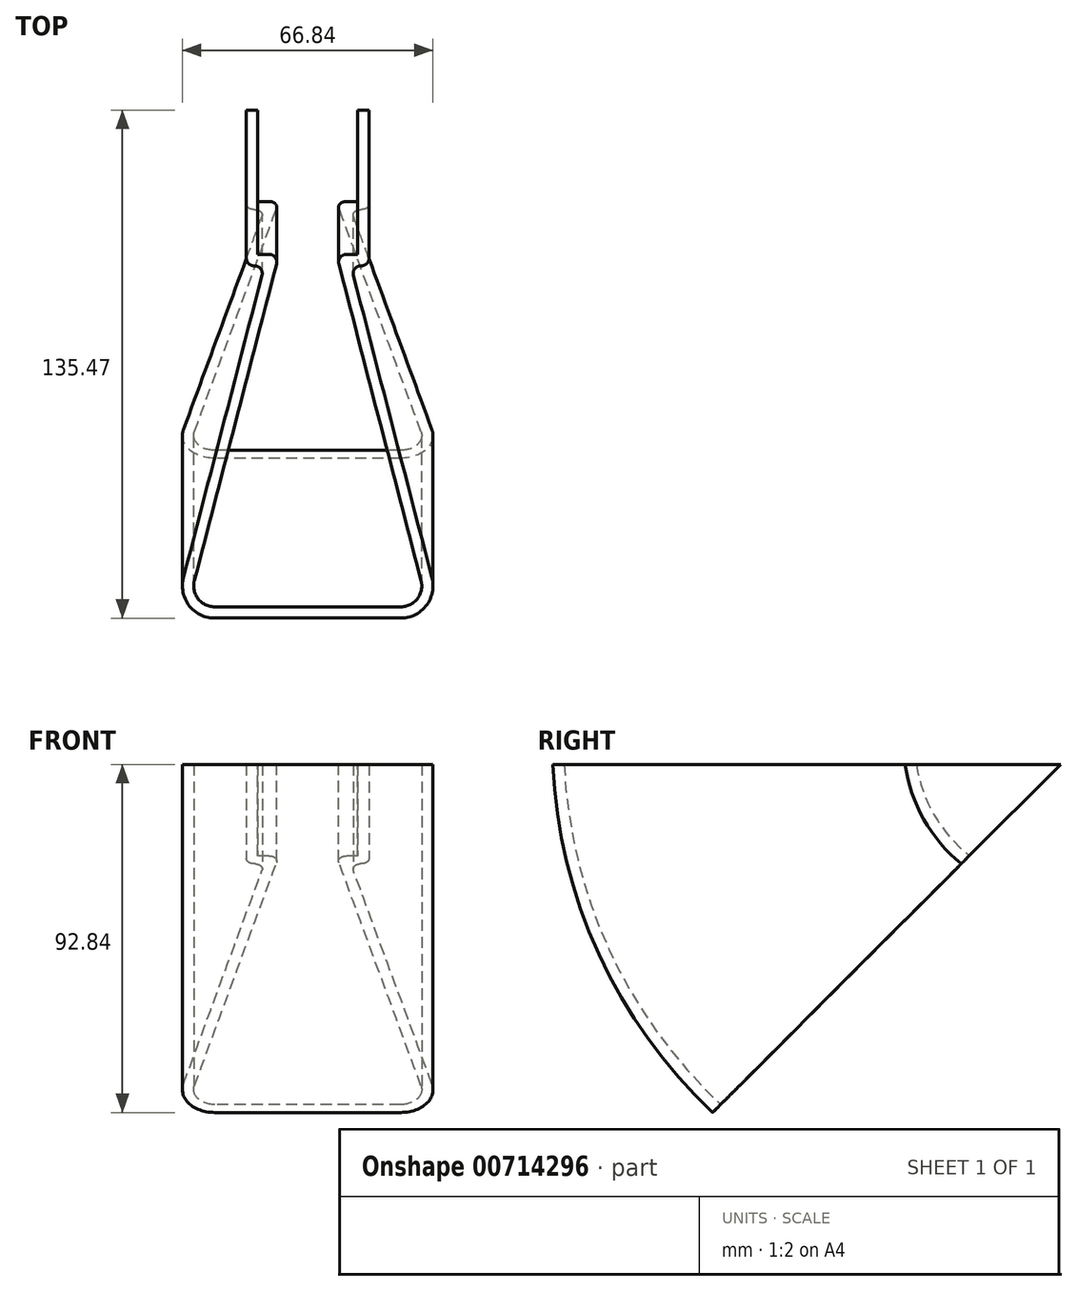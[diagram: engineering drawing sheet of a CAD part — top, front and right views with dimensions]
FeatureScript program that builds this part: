
annotation { "Feature Type Name" : "Feature", "Feature Type Description" : "" }
export const myFeature = defineFeature(function(context is Context, id is Id, definition is map)
    precondition{}
    {
        {
            var Q0;
            Q0=qCreatedBy(makeId("Top.planeOp"),FACE);
            var sketch = newSketch(context, id + "F0", { "sketchPlane" : qUnion([Q0])});
            skLineSegment(sketch, "E0", {"start": v(-5.5, 0) * mm, "end": v(5.5, 0) * mm, "construction": true});
            skLineSegment(sketch, "E1", {"start": v(-24.82, -94) * mm, "end": v(24.82, -94) * mm, "construction": true});
            skLineSegment(sketch, "E2", {"start": v(0, 0) * mm, "end": v(0, -94) * mm, "construction": true});
            skLineSegment(sketch, "E3", {"start": v(-5.5, 0) * mm, "end": v(-28.7, -89) * mm, "construction": true});
            skLineSegment(sketch, "E4", {"start": v(5.5, 0) * mm, "end": v(28.7, -89) * mm, "construction": true});
            skPoint(sketch, "E5.visualSharp", {"position": v(-30, -94) * mm});
            skArc(sketch, "E5.filletArc", {"start": v(-28.7, -89) * mm, "mid": v(-27.99, -92.45) * mm, "end": v(-24.82, -94) * mm, "construction": true});
            skPoint(sketch, "E6.visualSharp", {"position": v(30, -94) * mm});
            skArc(sketch, "E6.filletArc", {"start": v(24.82, -94) * mm, "mid": v(27.99, -92.45) * mm, "end": v(28.7, -89) * mm, "construction": true});
            skLineSegment(sketch, "E7.0", {"start": v(7.68, -2.03) * mm, "end": v(30.24, -88.59) * mm});
            skLineSegment(sketch, "E7.1", {"start": v(-7.68, -2.03) * mm, "end": v(-30.24, -88.59) * mm});
            skArc(sketch, "E7.2", {"start": v(-30.24, -88.59) * mm, "mid": v(-29.25, -93.42) * mm, "end": v(-24.82, -95.6) * mm});
            skLineSegment(sketch, "E7.3", {"start": v(-24.82, -95.6) * mm, "end": v(24.82, -95.6) * mm});
            skArc(sketch, "E7.4", {"start": v(24.82, -95.6) * mm, "mid": v(29.25, -93.42) * mm, "end": v(30.24, -88.59) * mm});
            skLineSegment(sketch, "E8", {"start": v(-5.5, 0) * mm, "end": v(-7.15, 0) * mm, "construction": true});
            skLineSegment(sketch, "E9", {"start": v(5.5, 0) * mm, "end": v(7.15, 0) * mm, "construction": true});
            skLineSegment(sketch, "E10.0", {"start": v(11.54, -4.95) * mm, "end": v(33.15, -87.83) * mm});
            skLineSegment(sketch, "E10.1", {"start": v(-11.54, -4.95) * mm, "end": v(-33.15, -87.83) * mm});
            skArc(sketch, "E10.2", {"start": v(-33.15, -87.83) * mm, "mid": v(-31.63, -95.26) * mm, "end": v(-24.82, -98.6) * mm});
            skLineSegment(sketch, "E10.3", {"start": v(-24.82, -98.6) * mm, "end": v(24.82, -98.6) * mm});
            skArc(sketch, "E10.4", {"start": v(24.82, -98.6) * mm, "mid": v(31.63, -95.26) * mm, "end": v(33.15, -87.83) * mm});
            skLineSegment(sketch, "E11", {"start": v(7.15, 0) * mm, "end": v(10.25, 0) * mm, "construction": true});
            skLineSegment(sketch, "E12", {"start": v(0, 0) * mm, "end": v(0, 37) * mm, "construction": true});
            skLineSegment(sketch, "E13", {"start": v(-19.77, 37) * mm, "end": v(21.2, 37) * mm, "construction": true});
            skLineSegment(sketch, "E14", {"start": v(10.25, 0) * mm, "end": v(11.75, 0) * mm, "construction": true});
            skLineSegment(sketch, "E15", {"start": v(11.75, 0) * mm, "end": v(11.75, 37) * mm, "construction": true});
            skLineSegment(sketch, "E16.0", {"start": v(5.5, 0) * mm, "end": v(6.32, 0) * mm});
            skLineSegment(sketch, "E16.1", {"start": v(-5.5, 0) * mm, "end": v(5.5, 0) * mm});
            skLineSegment(sketch, "E17.0", {"start": v(13.35, -1.95) * mm, "end": v(13.35, 37) * mm});
            skLineSegment(sketch, "E17.3", {"start": v(7.68, -2.03) * mm, "end": v(9.62, -1.95) * mm});
            skLineSegment(sketch, "E17.4", {"start": v(9.62, -1.95) * mm, "end": v(13.35, -1.95) * mm});
            skLineSegment(sketch, "E18.0", {"start": v(16.35, -4.95) * mm, "end": v(16.35, 37) * mm});
            skLineSegment(sketch, "E18.4", {"start": v(11.54, -4.95) * mm, "end": v(16.35, -4.95) * mm});
            skLineSegment(sketch, "E19", {"start": v(16.35, 37) * mm, "end": v(13.35, 37) * mm});
            skLineSegment(sketch, "E20.MirrorCS", {"start": v(-16.35, -4.95) * mm, "end": v(-16.35, 37) * mm});
            skLineSegment(sketch, "E21.MirrorCS", {"start": v(-13.35, -1.95) * mm, "end": v(-13.35, 37) * mm});
            skLineSegment(sketch, "E22.MirrorCS", {"start": v(-9.62, -1.95) * mm, "end": v(-13.35, -1.95) * mm});
            skLineSegment(sketch, "E23.MirrorCS", {"start": v(-11.54, -4.95) * mm, "end": v(-16.35, -4.95) * mm});
            skLineSegment(sketch, "E24.MirrorCS", {"start": v(-7.68, -2.03) * mm, "end": v(-9.62, -1.95) * mm});
            skLineSegment(sketch, "E25.MirrorCS", {"start": v(-16.35, 37) * mm, "end": v(-13.35, 37) * mm});
            skPoint(sketch, "E26.trimOffspring.end.orphan", {"position": v(9.62, -4.95) * mm});
            skPoint(sketch, "E26.trimOffspring.start.orphan", {"position": v(8.34, -4.57) * mm});
            skPoint(sketch, "E27.orphan", {"position": v(-9.62, -4.95) * mm});
            skPoint(sketch, "E28.MirrorCS.start.orphan", {"position": v(-8.34, -4.57) * mm});
            skSolve(sketch);
        }
        {
            var Q0;
            Q0=makeQuery(id+"F0.imprint","IMPRINT",FACE,{"disambiguationData":[TD([[makeQuery(id+"F0.imprint","IMPRINT",EDGE,{"derivedFrom":sQuery(id+"F0.wireOp",EDGE,"E7.0")}),1.0]])]});
            var Q1;
            Q1=sQuery(id+"F0.wireOp",EDGE,"E13");
            revolve(context, id + "F1", {"surfaceOperationType" : NewSurfaceOperationType.NEW, "entities" : qUnion([Q0]), "axis" : qUnion([Q1]), "revolveType" : RevolveType.TWO_DIRECTIONS, "angle" : 90 * degree, "angleBack" : 330 * degree});
        }
        {
            var Q0;
            Q0=makeQuery(id+"F1.opRevolve","SWEPT_EDGE",EDGE,{"disambiguationData":[OSD([sQuery(id+"F0.wireOp",EDGE,"E7.0"),sQuery(id+"F0.wireOp",EDGE,"E17.3")])]});
            var Q1;
            Q1=makeQuery(id+"F1.opRevolve","SWEPT_EDGE",EDGE,{"disambiguationData":[OSD([sQuery(id+"F0.wireOp",EDGE,"E10.0"),sQuery(id+"F0.wireOp",EDGE,"E18.4")])]});
            var Q2;
            Q2=makeQuery(id+"F1.opRevolve","SWEPT_EDGE",EDGE,{"disambiguationData":[OSD([sQuery(id+"F0.wireOp",EDGE,"E18.0"),sQuery(id+"F0.wireOp",EDGE,"E18.4")])]});
            var Q3;
            Q3=makeQuery(id+"F1.opRevolve","SWEPT_EDGE",EDGE,{"disambiguationData":[OSD([sQuery(id+"F0.wireOp",EDGE,"E7.1"),sQuery(id+"F0.wireOp",EDGE,"E24.MirrorCS")])]});
            var Q4;
            Q4=makeQuery(id+"F1.opRevolve","SWEPT_EDGE",EDGE,{"disambiguationData":[OSD([sQuery(id+"F0.wireOp",EDGE,"E20.MirrorCS"),sQuery(id+"F0.wireOp",EDGE,"E23.MirrorCS")])]});
            var Q5;
            Q5=makeQuery(id+"F1.opRevolve","SWEPT_EDGE",EDGE,{"disambiguationData":[OSD([sQuery(id+"F0.wireOp",EDGE,"E10.1"),sQuery(id+"F0.wireOp",EDGE,"E23.MirrorCS")])]});
            fillet(context, id + "F2", {"entities" : qUnion([Q0, Q1, Q2, Q3, Q4, Q5]), "radius" : 2 * mm, "tangentPropagation" : true, "allowEdgeOverflow" : false});
        }
        {
            var Q0;
            Q0=qCreatedBy(makeId("Right.planeOp"),FACE);
            var sketch = newSketch(context, id + "F3", { "sketchPlane" : qUnion([Q0])});
            skLineSegment(sketch, "E29.0", {"start": v(2.4, 19.98) * mm, "end": v(37, 0) * mm});
            skLineSegment(sketch, "E30.0", {"start": v(37, -39.95) * mm, "end": v(37, 0) * mm});
            skLineSegment(sketch, "E31", {"start": v(37, 0) * mm, "end": v(46.59, 0) * mm, "construction": true});
            skCircle(sketch, "E32", {"center": v(37, 0) * mm, "radius": 2.75 * mm});
            skPoint(sketch, "E33", {"position": v(44.9, 0) * mm});
            skCircle(sketch, "E34", {"center": v(44.9, 0) * mm, "radius": 2.65 * mm});
            skLineSegment(sketch, "E35", {"start": v(43.95, 2.47) * mm, "end": v(43.95, 0.95) * mm});
            skLineSegment(sketch, "E36", {"start": v(45.85, 2.47) * mm, "end": v(45.85, 0.95) * mm});
            skLineSegment(sketch, "E37", {"start": v(47.37, 0.95) * mm, "end": v(45.85, 0.95) * mm});
            skLineSegment(sketch, "E38", {"start": v(47.37, -0.95) * mm, "end": v(45.85, -0.95) * mm});
            skLineSegment(sketch, "E39.trimOffspring", {"start": v(45.85, -0.95) * mm, "end": v(45.85, -2.47) * mm});
            skLineSegment(sketch, "E40.trimOffspring", {"start": v(43.95, -0.95) * mm, "end": v(42.43, -0.95) * mm});
            skLineSegment(sketch, "E41.trimOffspring", {"start": v(43.95, -0.95) * mm, "end": v(43.95, -2.47) * mm});
            skLineSegment(sketch, "E42.trimOffspring", {"start": v(43.95, 0.95) * mm, "end": v(42.43, 0.95) * mm});
            skPoint(sketch, "E43", {"position": v(29.1, 0) * mm});
            skCircle(sketch, "E44", {"center": v(29.1, 0) * mm, "radius": 2.65 * mm});
            skLineSegment(sketch, "E45", {"start": v(28.15, 2.47) * mm, "end": v(28.15, 0.95) * mm});
            skLineSegment(sketch, "E46", {"start": v(30.05, 2.47) * mm, "end": v(30.05, 0.95) * mm});
            skLineSegment(sketch, "E47", {"start": v(31.57, 0.95) * mm, "end": v(30.05, 0.95) * mm});
            skLineSegment(sketch, "E48", {"start": v(31.57, -0.95) * mm, "end": v(30.05, -0.95) * mm});
            skLineSegment(sketch, "E49.trimOffspring", {"start": v(30.05, -0.95) * mm, "end": v(30.05, -2.47) * mm});
            skLineSegment(sketch, "E50.trimOffspring", {"start": v(28.15, -0.95) * mm, "end": v(26.63, -0.95) * mm});
            skLineSegment(sketch, "E51.trimOffspring", {"start": v(28.15, -0.95) * mm, "end": v(28.15, -2.47) * mm});
            skLineSegment(sketch, "E52.trimOffspring", {"start": v(28.15, 0.95) * mm, "end": v(26.63, 0.95) * mm});
            skLineSegment(sketch, "E53", {"start": v(26.6, 6) * mm, "end": v(51.55, 6) * mm});
            skLineSegment(sketch, "E54", {"start": v(51.55, 6) * mm, "end": v(51.55, -6) * mm});
            skLineSegment(sketch, "E55", {"start": v(51.55, -6) * mm, "end": v(37, -6) * mm});
            skLineSegment(sketch, "E56", {"start": v(26.6, 6) * mm, "end": v(22.45, 6) * mm});
            skLineSegment(sketch, "E57", {"start": v(22.45, 6) * mm, "end": v(22.45, -6) * mm});
            skLineSegment(sketch, "E58", {"start": v(22.45, -6) * mm, "end": v(37, -6) * mm});
            skSolve(sketch);
        }
        {
            var Q0;
            Q0 = qSketchRegion(id + "F3", true);
            var Q1;
            {var subQ0=sQuery(id+"F3.wireOp",EDGE,"E35");Q1=makeQuery(id+"F3.imprint","IMPRINT",FACE,{"disambiguationData":[TD([[makeQuery(id+"F3.imprint","IMPRINT",EDGE,{"derivedFrom":subQ0}),-1.0]])]});}
            var Q2;
            {var subQ0=sQuery(id+"F3.wireOp",EDGE,"E36");Q2=makeQuery(id+"F3.imprint","IMPRINT",FACE,{"disambiguationData":[TD([[makeQuery(id+"F3.imprint","IMPRINT",EDGE,{"derivedFrom":subQ0}),1.0]])]});}
            var Q3;
            {var subQ0=sQuery(id+"F3.wireOp",EDGE,"E38");Q3=makeQuery(id+"F3.imprint","IMPRINT",FACE,{"disambiguationData":[TD([[makeQuery(id+"F3.imprint","IMPRINT",EDGE,{"derivedFrom":subQ0}),1.0]])]});}
            var Q4;
            {var subQ0=sQuery(id+"F3.wireOp",EDGE,"E40.trimOffspring");Q4=makeQuery(id+"F3.imprint","IMPRINT",FACE,{"disambiguationData":[TD([[makeQuery(id+"F3.imprint","IMPRINT",EDGE,{"derivedFrom":subQ0}),1.0]])]});}
            var Q5;
            {var subQ0=sQuery(id+"F3.wireOp",EDGE,"E46");Q5=makeQuery(id+"F3.imprint","IMPRINT",FACE,{"disambiguationData":[TD([[makeQuery(id+"F3.imprint","IMPRINT",EDGE,{"derivedFrom":subQ0}),1.0]])]});}
            var Q6;
            {var subQ0=sQuery(id+"F3.wireOp",EDGE,"E45");Q6=makeQuery(id+"F3.imprint","IMPRINT",FACE,{"disambiguationData":[TD([[makeQuery(id+"F3.imprint","IMPRINT",EDGE,{"derivedFrom":subQ0}),-1.0]])]});}
            var Q7;
            {var subQ0=sQuery(id+"F3.wireOp",EDGE,"E50.trimOffspring");Q7=makeQuery(id+"F3.imprint","IMPRINT",FACE,{"disambiguationData":[TD([[makeQuery(id+"F3.imprint","IMPRINT",EDGE,{"derivedFrom":subQ0}),1.0]])]});}
            var Q8;
            {var subQ0=sQuery(id+"F3.wireOp",EDGE,"E48");Q8=makeQuery(id+"F3.imprint","IMPRINT",FACE,{"disambiguationData":[TD([[makeQuery(id+"F3.imprint","IMPRINT",EDGE,{"derivedFrom":subQ0}),1.0]])]});}
            extrude(context, id + "F4", {"entities" : qUnion([Q0, Q1, Q2, Q3, Q4, Q5, Q6, Q7, Q8]), "operationType" : NewBodyOperationType.ADD, "depth" : 25 * mm, "offsetDistance" : 25 * mm, "hasSecondDirection" : true, "secondDirectionOppositeDirection" : true, "secondDirectionDepth" : 25 * mm});
        }
        {
            var Q0;
            {var subQ0=sQuery(id+"F3.wireOp",EDGE,"E30.0");var subQ1=sQuery(id+"F3.wireOp",EDGE,"E29.0");var subQ2=makeQuery(id+"F3.imprint","INTERSECT",VERTEX,{"derivedFrom":[subQ1,subQ0]});Q0=makeQuery(id+"F3.imprint","IMPRINT",FACE,{"disambiguationData":[TD([[makeQuery(id+"F3.imprint","IMPRINT",EDGE,{"disambiguationData":[TD([[subQ2,1.0]])],"derivedFrom":subQ1}),-1.0]])]});}
            var Q1;
            {var subQ4=sQuery(id+"F3.wireOp",EDGE,"E45");Q1=makeQuery(id+"F3.imprint","IMPRINT",FACE,{"disambiguationData":[TD([[makeQuery(id+"F3.imprint","IMPRINT",EDGE,{"derivedFrom":subQ4}),1.0]])]});}
            extrude(context, id + "F5", {"entities" : qUnion([Q0, Q1]), "operationType" : NewBodyOperationType.REMOVE, "oppositeDirection" : true, "depth" : 25 * mm, "offsetDistance" : 25 * mm, "hasSecondDirection" : true, "secondDirectionOppositeDirection" : false, "secondDirectionDepth" : 25 * mm});
        }
        {
            var Q0;
            Q0=qCreatedBy(makeId("Top.planeOp"),FACE);
            var sketch = newSketch(context, id + "F6", { "sketchPlane" : qUnion([Q0])});
            skLineSegment(sketch, "E59.0", {"start": v(-13.35, 17.7) * mm, "end": v(-13.35, 33.54) * mm});
            skLineSegment(sketch, "E60.0", {"start": v(13.35, 17.7) * mm, "end": v(13.35, 33.54) * mm});
            skLineSegment(sketch, "E61", {"start": v(-13.35, 33.54) * mm, "end": v(-13.35, 53.62) * mm});
            skLineSegment(sketch, "E62", {"start": v(-13.35, 53.62) * mm, "end": v(12.83, 52.58) * mm});
            skLineSegment(sketch, "E63", {"start": v(13.35, 33.54) * mm, "end": v(13.35, 51.84) * mm});
            skLineSegment(sketch, "E64", {"start": v(13.35, 51.84) * mm, "end": v(12.83, 52.58) * mm});
            skLineSegment(sketch, "E65", {"start": v(-13.35, 17.7) * mm, "end": v(13.35, 17.7) * mm});
            skLineSegment(sketch, "E66", {"start": v(-13.35, 33.54) * mm, "end": v(-21.25, 33.54) * mm});
            skLineSegment(sketch, "E67", {"start": v(-21.25, 21.16) * mm, "end": v(-21.25, 81.34) * mm});
            skLineSegment(sketch, "E68", {"start": v(-21.25, 81.34) * mm, "end": v(-34.78, 11.59) * mm});
            skLineSegment(sketch, "E69", {"start": v(-34.78, 11.59) * mm, "end": v(-21.25, 21.16) * mm});
            skLineSegment(sketch, "E70.MirrorCS", {"start": v(34.78, 11.59) * mm, "end": v(21.25, 21.16) * mm});
            skLineSegment(sketch, "E71.MirrorCS", {"start": v(21.25, 81.34) * mm, "end": v(34.78, 11.59) * mm});
            skLineSegment(sketch, "E72.MirrorCS", {"start": v(21.25, 21.16) * mm, "end": v(21.25, 81.34) * mm});
            skSolve(sketch);
        }
        {
            var Q0;
            Q0 = qSketchRegion(id + "F6", true);
            extrude(context, id + "F7", {"entities" : qUnion([Q0]), "operationType" : NewBodyOperationType.REMOVE, "oppositeDirection" : true, "depth" : 25 * mm, "offsetDistance" : 25 * mm, "hasSecondDirection" : true, "secondDirectionOppositeDirection" : false, "secondDirectionDepth" : 25 * mm});
        }
        {
            var Q0;
            {var subQ0=sQuery(id+"F3.wireOp",EDGE,"E58");var subQ1=sQuery(id+"F3.wireOp",EDGE,"E57");Q0=makeQuery(id+"F4.boolean.opBoolean","SPLIT",EDGE,{"disambiguationData":[TD([makeQuery(id+"F1.opRevolve","SWEPT_FACE",FACE,{"disambiguationData":[OSD([sQuery(id+"F0.wireOp",EDGE,"E20.MirrorCS")])]})])],"derivedFrom":makeQuery(id+"F4.opExtrude","SWEPT_EDGE",EDGE,{"disambiguationData":[OSD([subQ1,subQ0])]})});}
            var Q1;
            {var subQ0=sQuery(id+"F3.wireOp",EDGE,"E56");var subQ2=sQuery(id+"F3.wireOp",EDGE,"E57");Q1=makeQuery(id+"F4.boolean.opBoolean","SPLIT",EDGE,{"disambiguationData":[TD([makeQuery(id+"F1.opRevolve","SWEPT_FACE",FACE,{"disambiguationData":[OSD([sQuery(id+"F0.wireOp",EDGE,"E20.MirrorCS")])]})])],"derivedFrom":makeQuery(id+"F4.opExtrude","SWEPT_EDGE",EDGE,{"disambiguationData":[OSD([subQ0,subQ2])]})});}
            var Q2;
            {var subQ0=sQuery(id+"F3.wireOp",EDGE,"E53");var subQ1=sQuery(id+"F3.wireOp",EDGE,"E54");Q2=makeQuery(id+"F7.boolean.opBoolean","SPLIT",EDGE,{"disambiguationData":[TD([makeQuery(id+"F1.opRevolve","SWEPT_FACE",FACE,{"disambiguationData":[OSD([sQuery(id+"F0.wireOp",EDGE,"E21.MirrorCS")])]})])],"derivedFrom":makeQuery(id+"F4.opExtrude","SWEPT_EDGE",EDGE,{"disambiguationData":[OSD([subQ0,subQ1])]})});}
            var Q3;
            {var subQ0=sQuery(id+"F3.wireOp",EDGE,"E55");var subQ1=sQuery(id+"F3.wireOp",EDGE,"E54");Q3=makeQuery(id+"F7.boolean.opBoolean","SPLIT",EDGE,{"disambiguationData":[TD([makeQuery(id+"F1.opRevolve","SWEPT_FACE",FACE,{"disambiguationData":[OSD([sQuery(id+"F0.wireOp",EDGE,"E21.MirrorCS")])]})])],"derivedFrom":makeQuery(id+"F4.opExtrude","SWEPT_EDGE",EDGE,{"disambiguationData":[OSD([subQ1,subQ0])]})});}
            var Q4;
            {var subQ0=sQuery(id+"F3.wireOp",EDGE,"E55");var subQ1=sQuery(id+"F3.wireOp",EDGE,"E54");Q4=makeQuery(id+"F7.boolean.opBoolean","SPLIT",EDGE,{"disambiguationData":[TD([makeQuery(id+"F1.opRevolve","SWEPT_FACE",FACE,{"disambiguationData":[OSD([sQuery(id+"F0.wireOp",EDGE,"E17.0")])]})])],"derivedFrom":makeQuery(id+"F4.opExtrude","SWEPT_EDGE",EDGE,{"disambiguationData":[OSD([subQ1,subQ0])]})});}
            var Q5;
            {var subQ0=sQuery(id+"F3.wireOp",EDGE,"E53");var subQ1=sQuery(id+"F3.wireOp",EDGE,"E54");Q5=makeQuery(id+"F7.boolean.opBoolean","SPLIT",EDGE,{"disambiguationData":[TD([makeQuery(id+"F1.opRevolve","SWEPT_FACE",FACE,{"disambiguationData":[OSD([sQuery(id+"F0.wireOp",EDGE,"E17.0")])]})])],"derivedFrom":makeQuery(id+"F4.opExtrude","SWEPT_EDGE",EDGE,{"disambiguationData":[OSD([subQ0,subQ1])]})});}
            var Q6;
            {var subQ0=sQuery(id+"F3.wireOp",EDGE,"E57");var subQ1=sQuery(id+"F3.wireOp",EDGE,"E56");Q6=makeQuery(id+"F4.boolean.opBoolean","SPLIT",EDGE,{"disambiguationData":[TD([makeQuery(id+"F1.opRevolve","SWEPT_FACE",FACE,{"disambiguationData":[OSD([sQuery(id+"F0.wireOp",EDGE,"E18.0")])]})])],"derivedFrom":makeQuery(id+"F4.opExtrude","SWEPT_EDGE",EDGE,{"disambiguationData":[OSD([subQ1,subQ0])]})});}
            var Q7;
            {var subQ0=sQuery(id+"F3.wireOp",EDGE,"E57");var subQ1=sQuery(id+"F3.wireOp",EDGE,"E58");Q7=makeQuery(id+"F4.boolean.opBoolean","SPLIT",EDGE,{"disambiguationData":[TD([makeQuery(id+"F1.opRevolve","SWEPT_FACE",FACE,{"disambiguationData":[OSD([sQuery(id+"F0.wireOp",EDGE,"E18.0")])]})])],"derivedFrom":makeQuery(id+"F4.opExtrude","SWEPT_EDGE",EDGE,{"disambiguationData":[OSD([subQ0,subQ1])]})});}
            fillet(context, id + "F8", {"entities" : qUnion([Q0, Q1, Q2, Q3, Q4, Q5, Q6, Q7]), "radius" : 5 * mm, "tangentPropagation" : true, "allowEdgeOverflow" : false});
        }
        {
            var Q0;
            Q0=qCreatedBy(makeId("Right.planeOp"),FACE);
            var sketch = newSketch(context, id + "F9", { "sketchPlane" : qUnion([Q0])});
            skLineSegment(sketch, "E73.0", {"start": v(27.45, -6) * mm, "end": v(46.55, -6) * mm});
            skLineSegment(sketch, "E74", {"start": v(27.45, -6) * mm, "end": v(-115.04, -6) * mm});
            skLineSegment(sketch, "E75", {"start": v(-115.04, -6) * mm, "end": v(-90.25, -115.48) * mm});
            skLineSegment(sketch, "E76", {"start": v(-90.25, -115.48) * mm, "end": v(34.87, -144.84) * mm});
            skLineSegment(sketch, "E77", {"start": v(34.87, -144.84) * mm, "end": v(87.64, -115.48) * mm});
            skLineSegment(sketch, "E78", {"start": v(87.64, -115.48) * mm, "end": v(89.77, -48.66) * mm});
            skLineSegment(sketch, "E79", {"start": v(89.77, -48.66) * mm, "end": v(46.55, -6) * mm});
            skLineSegment(sketch, "E80", {"start": v(89.77, -48.66) * mm, "end": v(83.26, 31.43) * mm});
            skLineSegment(sketch, "E81", {"start": v(83.26, 31.43) * mm, "end": v(-50.02, 71.41) * mm});
            skLineSegment(sketch, "E82", {"start": v(-50.02, 71.41) * mm, "end": v(-90, 71.41) * mm});
            skLineSegment(sketch, "E83", {"start": v(-90, 71.41) * mm, "end": v(-115.04, -6) * mm});
            skSolve(sketch);
        }
        {
            var Q0;
            Q0=makeQuery(id+"F9.imprint","IMPRINT",FACE,{"disambiguationData":[TD([[makeQuery(id+"F9.imprint","IMPRINT",EDGE,{"derivedFrom":sQuery(id+"F9.wireOp",EDGE,"E73.0")}),1.0]])]});
            extrude(context, id + "F10", {"entities" : qUnion([Q0]), "operationType" : NewBodyOperationType.REMOVE, "endBound" : BoundingType.THROUGH_ALL, "depth" : 25 * mm, "offsetDistance" : 25 * mm, "hasSecondDirection" : true, "secondDirectionBound" : SecondDirectionBoundingType.THROUGH_ALL, "secondDirectionOppositeDirection" : true, "secondDirectionDepth" : 25 * mm});
        }
        {
            var Q0;
            Q0=qCreatedBy(makeId("Right.planeOp"),FACE);
            var sketch = newSketch(context, id + "F11", { "sketchPlane" : qUnion([Q0])});
            skLineSegment(sketch, "E84.0", {"start": v(37, -6) * mm, "end": v(-2.5, -6) * mm, "construction": true});
            skLineSegment(sketch, "E85.0", {"start": v(37, -39.95) * mm, "end": v(37, -6) * mm, "construction": true});
            skLineSegment(sketch, "E86", {"start": v(37, -6) * mm, "end": v(-77.38, -120.38) * mm});
            skLineSegment(sketch, "E87", {"start": v(-77.38, -120.38) * mm, "end": v(-35.6, -136.92) * mm});
            skLineSegment(sketch, "E88", {"start": v(-35.6, -136.92) * mm, "end": v(64.66, -143.49) * mm});
            skLineSegment(sketch, "E89", {"start": v(64.66, -143.49) * mm, "end": v(76.95, -111.27) * mm});
            skLineSegment(sketch, "E90", {"start": v(76.95, -111.27) * mm, "end": v(76.95, -24.8) * mm});
            skLineSegment(sketch, "E91", {"start": v(76.95, -24.8) * mm, "end": v(57.03, 8.69) * mm});
            skLineSegment(sketch, "E92", {"start": v(57.03, 8.69) * mm, "end": v(37, -6) * mm});
            skSolve(sketch);
        }
        {
            var Q0;
            Q0=makeQuery(id+"F11.imprint","IMPRINT",FACE,{"disambiguationData":[TD([[makeQuery(id+"F11.imprint","IMPRINT",EDGE,{"derivedFrom":sQuery(id+"F11.wireOp",EDGE,"E86")}),1.0]])]});
            extrude(context, id + "F12", {"entities" : qUnion([Q0]), "operationType" : NewBodyOperationType.REMOVE, "oppositeDirection" : true, "depth" : 50 * mm, "offsetDistance" : 25 * mm, "hasSecondDirection" : true, "secondDirectionOppositeDirection" : false, "secondDirectionDepth" : 50 * mm});
        }
    });
